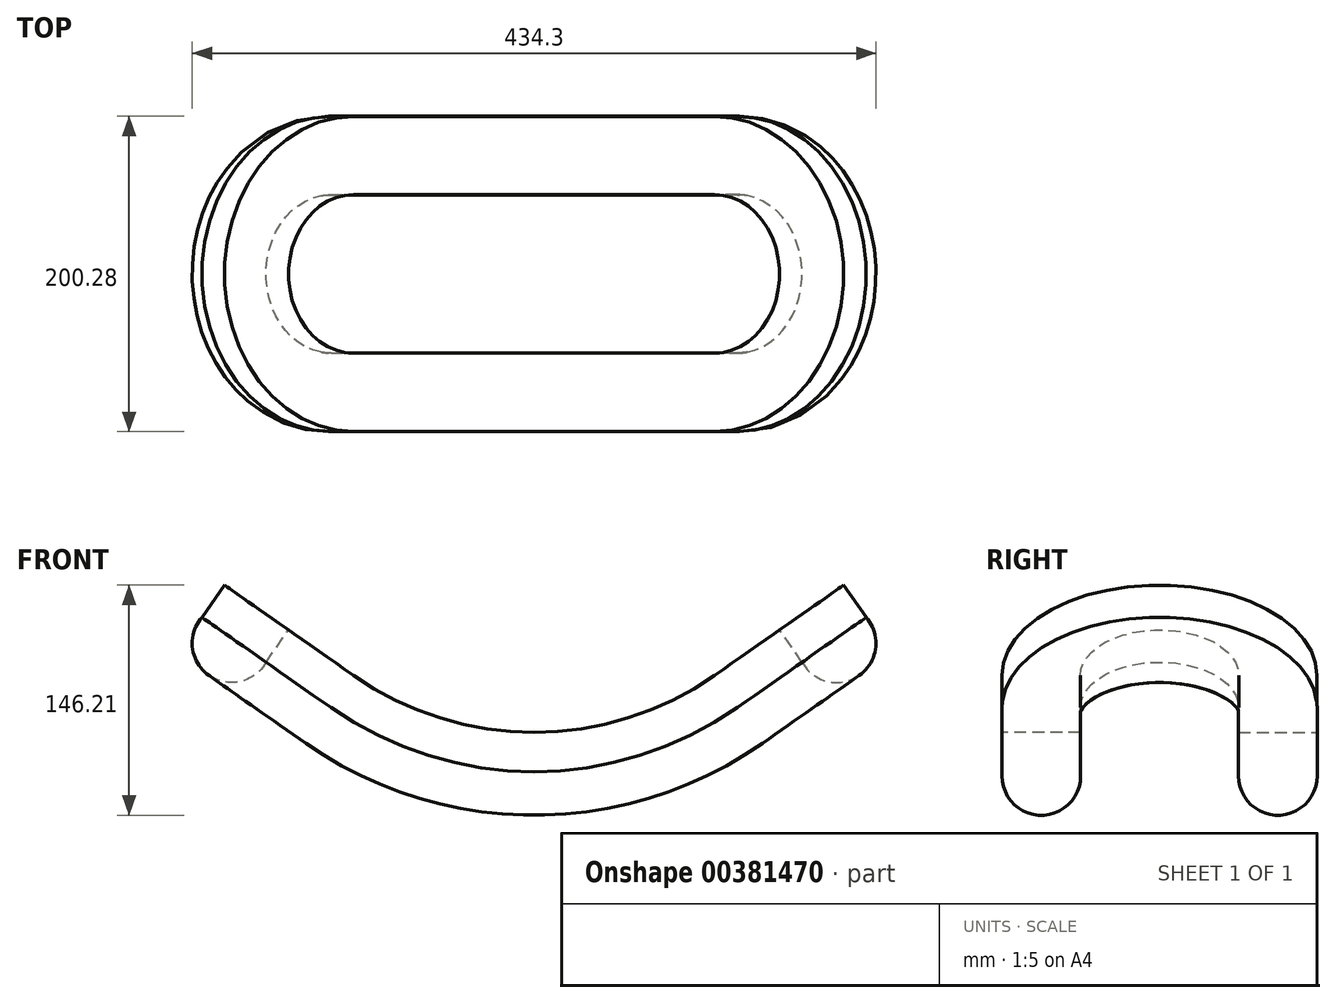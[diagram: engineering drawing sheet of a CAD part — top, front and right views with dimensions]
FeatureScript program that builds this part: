
annotation { "Feature Type Name" : "Feature", "Feature Type Description" : "" }
export const myFeature = defineFeature(function(context is Context, id is Id, definition is map)
    precondition{}
    {
        {
            var Q0;
            Q0=qCreatedBy(makeId("Front.planeOp"),FACE);
            var sketch = newSketch(context, id + "F0", { "sketchPlane" : qUnion([Q0])});
            skArc(sketch, "E0", {"start": v(0, 0) * mm, "mid": v(60.14, 9.26) * mm, "end": v(114.72, 36.17) * mm});
            skLineSegment(sketch, "E1", {"start": v(114.72, 36.17) * mm, "end": v(196.63, 93.53) * mm});
            skLineSegment(sketch, "E2", {"start": v(0, 200) * mm, "end": v(114.72, 36.17) * mm, "construction": true});
            skSolve(sketch);
        }
        {
            var Q0;
            Q0=sQuery(id+"F0.wireOp",EDGE,"E1");
            var Q1;
            Q1=sQuery(id+"F0.wireOp",EDGE,"E0");
            extrude(context, id + "F1", {"bodyType" : ToolBodyType.SURFACE, "surfaceEntities" : qUnion([Q0, Q1]), "depth" : 100 * mm});
        }
        {
            var Q0;
            Q0=makeQuery(id+"F1.opExtrude","SWEPT_FACE",FACE,{"disambiguationData":[OSD([sQuery(id+"F0.wireOp",EDGE,"E1")])]});
            var sketch = newSketch(context, id + "F2", { "sketchPlane" : qUnion([Q0])});
            skArc(sketch, "E3", {"start": v(214.72, 0) * mm, "mid": v(185.43, 70.71) * mm, "end": v(114.72, 100) * mm});
            skSolve(sketch);
        }
        {
            var Q0;
            Q0=qCreatedBy(makeId("Right.planeOp"),FACE);
            var sketch = newSketch(context, id + "F3", { "sketchPlane" : qUnion([Q0])});
            skLineSegment(sketch, "E4", {"start": v(-100, 0) * mm, "end": v(-100, -25) * mm});
            skArc(sketch, "E5", {"start": v(-100, -25) * mm, "mid": v(-75.14, -52.68) * mm, "end": v(-50.29, -25) * mm});
            skLineSegment(sketch, "E6", {"start": v(-50.29, -25) * mm, "end": v(-50.29, 0) * mm});
            skLineSegment(sketch, "E7", {"start": v(-100, 0) * mm, "end": v(-50.29, 0) * mm});
            skSolve(sketch);
        }
        {
            var Q0;
            Q0=makeQuery(id+"F3.imprint","IMPRINT",FACE,{"disambiguationData":[TD([[makeQuery(id+"F3.imprint","IMPRINT",EDGE,{"derivedFrom":sQuery(id+"F3.wireOp",EDGE,"E4")}),1.0]])]});
            var Q1;
            Q1=makeQuery(id+"F1.opExtrude","CAP_EDGE",EDGE,{"disambiguationData":[OSD([sQuery(id+"F0.wireOp",EDGE,"E0")])],"isStart":false});
            var Q2;
            Q2=sQuery(id+"F2.wireOp",EDGE,"E3");
            sweep(context, id + "F4", {"profiles" : qUnion([Q0]), "path" : qUnion([Q1, Q2])});
        }
        {
            var Q0;
            Q0=makeQuery(id+"F4.opSweep","SWEPT_BODY",BODY,{"disambiguationData":[OSD([sQuery(id+"F2.wireOp",EDGE,"E3"),sQuery(id+"F3.wireOp",EDGE,"E4"),sQuery(id+"F3.wireOp",EDGE,"E5"),sQuery(id+"F3.wireOp",EDGE,"E6"),sQuery(id+"F3.wireOp",EDGE,"E7")])]});
            var Q1;
            Q1=qCreatedBy(makeId("Front.planeOp"),FACE);
            mirror(context, id + "F5", {"operationType" : NewBodyOperationType.ADD, "entities" : qUnion([Q0]), "mirrorPlane" : qUnion([Q1])});
        }
        {
            var Q0;
            Q0=makeQuery(id+"F4.opSweep","SWEPT_BODY",BODY,{"disambiguationData":[OSD([sQuery(id+"F2.wireOp",EDGE,"E3"),sQuery(id+"F3.wireOp",EDGE,"E4"),sQuery(id+"F3.wireOp",EDGE,"E5"),sQuery(id+"F3.wireOp",EDGE,"E6"),sQuery(id+"F3.wireOp",EDGE,"E7")])]});
            var Q1;
            Q1=qCreatedBy(makeId("Right.planeOp"),FACE);
            mirror(context, id + "F6", {"operationType" : NewBodyOperationType.ADD, "entities" : qUnion([Q0]), "mirrorPlane" : qUnion([Q1])});
        }
    });
